# Revit family: IS_TonicII_K2909_BIM_DE
name_source: partatom
category: Plumbing Fixtures
revit_build: Autodesk Revit MEP 2016 (Build: 20161004_0715(x64)
units: mm (PartAtom-declared; Revit-internal decimal feet)

## family parameters
Always vertical = No
Cut with Voids When Loaded = No
Part Type = Normal
Room Calculation Point = No
Round Connector Dimension = Use Diameter
Shared = No
Work Plane-Based = No

## types (1)
- K290901 TONIC II double ended bath tub 2000x1000mm
    Accessories = www.idealstandard.de\ersatzteile
    BIMobject category = Bath & Spas
    BOSUseNativeGeometries = 1
    Brand = Ideal Standard
    Brand url = http://www.idealstandard.de
    Date of publishing = 20/12/2017
    DrainSize = 0 mm  [stored 0 ft]
    EAN code = https://4015413066419
    Edition number = 1
    IFC Classification = Sanitary Terminal
    Installation instructions = http://www.idealstandard.de
    Manufacturer name = Ideal Standard
    ManufacturerURL = http://www.idealstandard.de
    Material main = Acrylic
    MaterialThickness = 0 mm  [stored 0 ft]
    Model = K290901
    NBS Reference Code = 35-06-08
    NBS Reference Description = Baths
    Nominal height = 490
    Nominal width = 1000
    NominalDepth = 0 mm  [stored 0 ft]
    NominalHeight = 488 mm
    NominalLength = 2000 mm  [stored 6.56168 ft]
    NominalWidth = 1000 mm  [stored 3.28084 ft]
    OmniClass Code = 23-31 15 00
    OmniClass Description = Bathtubs
    Product Guid = 7770a618-d8f3-466a-8f9e-6be720a003cd
    Product SKU = K2909
    Product data url = https://bimobject.com
    Product family = TONIC II
    Product group = Bath Tub
    Product name = TONIC II double ended bath tub 2000x1000mm
    Product url = http://www.idealstandard.de
    ProductInformation = www.idealstandard.de/produkte
    QR code = http://bimobject.com
    Size = 2000x1000x488 mm
    Technical description = http://www.idealstandard.de
    URL = http://www.idealstandard.de
    Uniclass 1.4 Code = L7211
    Uniclass 1.4 Description = Baths
    Uniclass 2.0 Code = PR-35-06-08
    Uniclass 2.0 Description = Baths
    Uniclass 2015 Code = Pr_40_20_06_08
    Uniclass 2015 Name = Baths
    Weight Net (Kg) = 32.5

note: [stored X ft] marks values corroborated as IEEE doubles in the binary element streams (Revit-internal decimal feet)

## geometry (parser evidence)
native form markers: Blend x4, Sweep x1
no freeform markers — native parametric forms only
